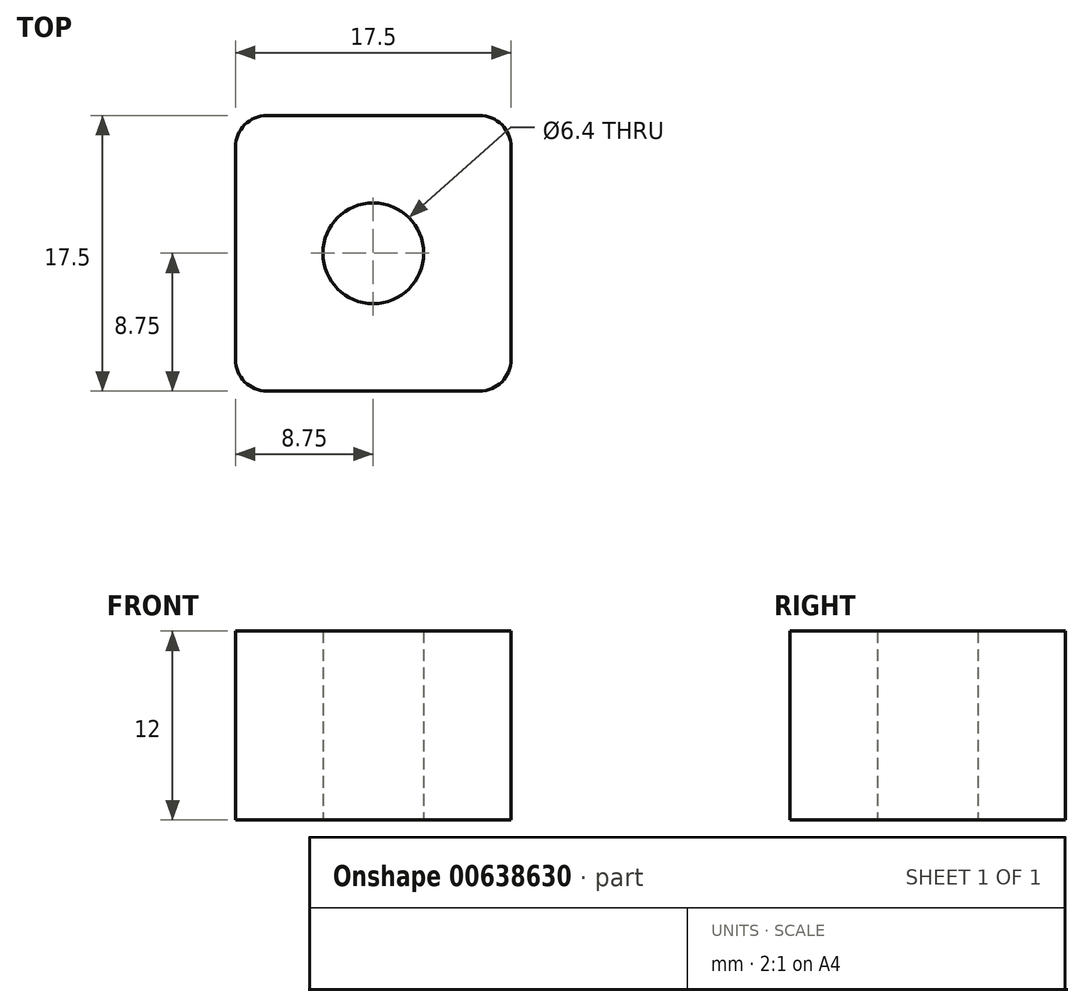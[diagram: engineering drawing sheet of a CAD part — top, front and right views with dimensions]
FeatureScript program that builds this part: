
annotation { "Feature Type Name" : "Feature", "Feature Type Description" : "" }
export const myFeature = defineFeature(function(context is Context, id is Id, definition is map)
    precondition{}
    {
        {
            var Q0;
            Q0=qCreatedBy(makeId("Top.planeOp"),FACE);
            var sketch = newSketch(context, id + "F0", { "sketchPlane" : qUnion([Q0])});
            skCircle(sketch, "E0", {"center": v(0, 0) * mm, "radius": 3.2 * mm});
            skLineSegment(sketch, "E1.bottom", {"start": v(-8.75, 8.75) * mm, "end": v(8.75, 8.75) * mm});
            skLineSegment(sketch, "E1.top", {"start": v(-8.75, -8.75) * mm, "end": v(8.75, -8.75) * mm});
            skLineSegment(sketch, "E1.left", {"start": v(-8.75, 8.75) * mm, "end": v(-8.75, -8.75) * mm});
            skLineSegment(sketch, "E1.right", {"start": v(8.75, 8.75) * mm, "end": v(8.75, -8.75) * mm});
            skPoint(sketch, "E2", {"position": v(0, 8.75) * mm});
            skPoint(sketch, "E3", {"position": v(-8.75, 0) * mm});
            skSolve(sketch);
        }
        {
            var Q0;
            Q0=makeQuery(id+"F0.imprint","IMPRINT",FACE,{"disambiguationData":[TD([[makeQuery(id+"F0.imprint","IMPRINT",EDGE,{"derivedFrom":sQuery(id+"F0.wireOp",EDGE,"E0")}),-1.0]])]});
            extrude(context, id + "F1", {"entities" : qUnion([Q0]), "depth" : 12 * mm, "offsetDistance" : 25 * mm});
        }
        {
            var Q0;
            Q0=makeQuery(id+"F1.opExtrude","SWEPT_EDGE",EDGE,{"disambiguationData":[OSD([sQuery(id+"F0.wireOp",EDGE,"E1.bottom"),sQuery(id+"F0.wireOp",EDGE,"E1.left")])]});
            var Q1;
            Q1=makeQuery(id+"F1.opExtrude","SWEPT_EDGE",EDGE,{"disambiguationData":[OSD([sQuery(id+"F0.wireOp",EDGE,"E1.bottom"),sQuery(id+"F0.wireOp",EDGE,"E1.right")])]});
            var Q2;
            Q2=makeQuery(id+"F1.opExtrude","SWEPT_EDGE",EDGE,{"disambiguationData":[OSD([sQuery(id+"F0.wireOp",EDGE,"E1.top"),sQuery(id+"F0.wireOp",EDGE,"E1.left")])]});
            var Q3;
            Q3=makeQuery(id+"F1.opExtrude","SWEPT_EDGE",EDGE,{"disambiguationData":[OSD([sQuery(id+"F0.wireOp",EDGE,"E1.top"),sQuery(id+"F0.wireOp",EDGE,"E1.right")])]});
            fillet(context, id + "F2", {"entities" : qUnion([Q0, Q1, Q2, Q3]), "radius" : 2 * mm, "tangentPropagation" : true, "allowEdgeOverflow" : false});
        }
    });
